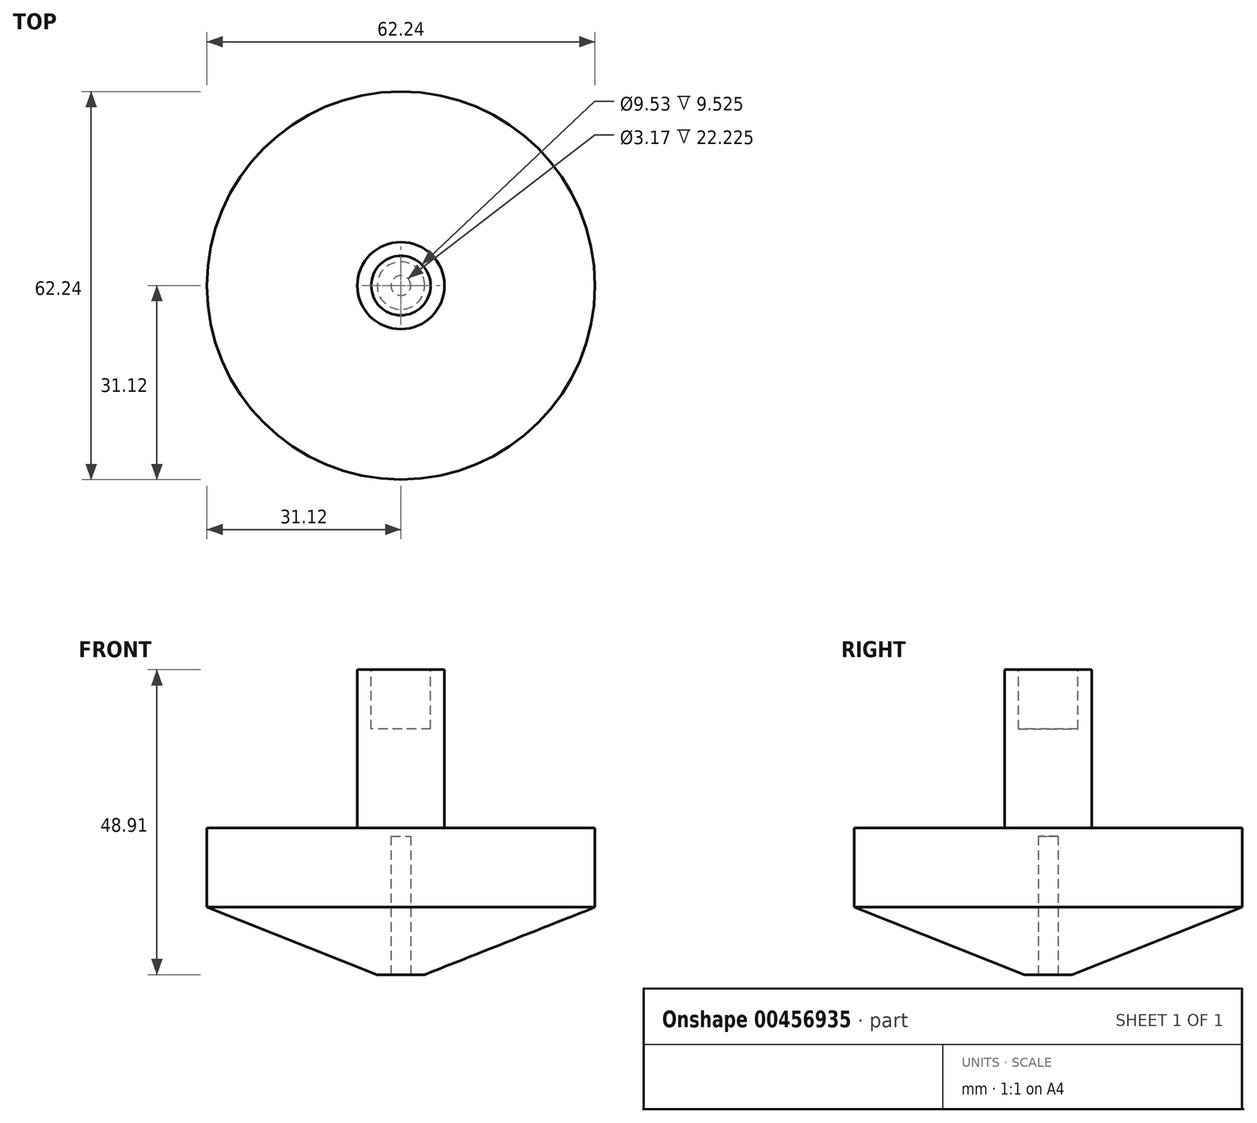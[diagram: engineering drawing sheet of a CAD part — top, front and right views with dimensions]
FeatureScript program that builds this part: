
annotation { "Feature Type Name" : "Feature", "Feature Type Description" : "" }
export const myFeature = defineFeature(function(context is Context, id is Id, definition is map)
    precondition{}
    {
        {
            var Q0;
            Q0=qCreatedBy(makeId("Front.planeOp"),FACE);
            var sketch = newSketch(context, id + "F0", { "sketchPlane" : qUnion([Q0])});
            skLineSegment(sketch, "E0", {"start": v(31.12, 12.7) * mm, "end": v(31.12, 25.4) * mm});
            skLineSegment(sketch, "E1", {"start": v(31.12, 25.4) * mm, "end": v(6.99, 25.4) * mm});
            skLineSegment(sketch, "E2", {"start": v(6.99, 25.4) * mm, "end": v(6.99, 50.8) * mm});
            skLineSegment(sketch, "E3", {"start": v(6.99, 50.8) * mm, "end": v(0, 50.8) * mm});
            skLineSegment(sketch, "E4", {"start": v(0, 50.8) * mm, "end": v(0, 1.89) * mm});
            skLineSegment(sketch, "E5", {"start": v(0, 1.89) * mm, "end": v(3.81, 1.89) * mm});
            skLineSegment(sketch, "E6", {"start": v(3.8, 1.89) * mm, "end": v(31.12, 12.7) * mm});
            skSolve(sketch);
        }
        {
            var Q0;
            Q0=makeQuery(id+"F0.imprint","IMPRINT",FACE,{"disambiguationData":[TD([[makeQuery(id+"F0.imprint","IMPRINT",EDGE,{"derivedFrom":sQuery(id+"F0.wireOp",EDGE,"E0")}),1.0]])]});
            var Q1;
            Q1=sQuery(id+"F0.wireOp",EDGE,"E4");
            revolve(context, id + "F1", {"entities" : qUnion([Q0]), "axis" : qUnion([Q1]), "revolveType" : RevolveType.FULL});
        }
        {
            var Q0;
            Q0=makeQuery(id+"F1.opRevolve","SWEPT_FACE",FACE,{"disambiguationData":[OSD([sQuery(id+"F0.wireOp",EDGE,"E3")])]});
            var sketch = newSketch(context, id + "F2", { "sketchPlane" : qUnion([Q0])});
            skCircle(sketch, "E7", {"center": v(0, 0) * mm, "radius": 4.76 * mm});
            skSolve(sketch);
        }
        {
            var Q0;
            Q0=makeQuery(id+"F2.imprint","IMPRINT",FACE,{"disambiguationData":[TD([[makeQuery(id+"F2.imprint","IMPRINT",EDGE,{"derivedFrom":sQuery(id+"F2.wireOp",EDGE,"E7")}),1.0]])]});
            extrude(context, id + "F3", {"entities" : qUnion([Q0]), "operationType" : NewBodyOperationType.REMOVE, "oppositeDirection" : true, "depth" : 9.52 * mm});
        }
        {
            var Q0;
            Q0=makeQuery(id+"F1.opRevolve","SWEPT_FACE",FACE,{"disambiguationData":[OSD([sQuery(id+"F0.wireOp",EDGE,"E5")])]});
            var sketch = newSketch(context, id + "F4", { "sketchPlane" : qUnion([Q0])});
            skCircle(sketch, "E8", {"center": v(0, 0) * mm, "radius": 1.59 * mm});
            skSolve(sketch);
        }
        {
            var Q0;
            Q0 = qSketchRegion(id + "F4", true);
            extrude(context, id + "F5", {"entities" : qUnion([Q0]), "operationType" : NewBodyOperationType.REMOVE, "oppositeDirection" : true, "depth" : 22.22 * mm});
        }
    });
